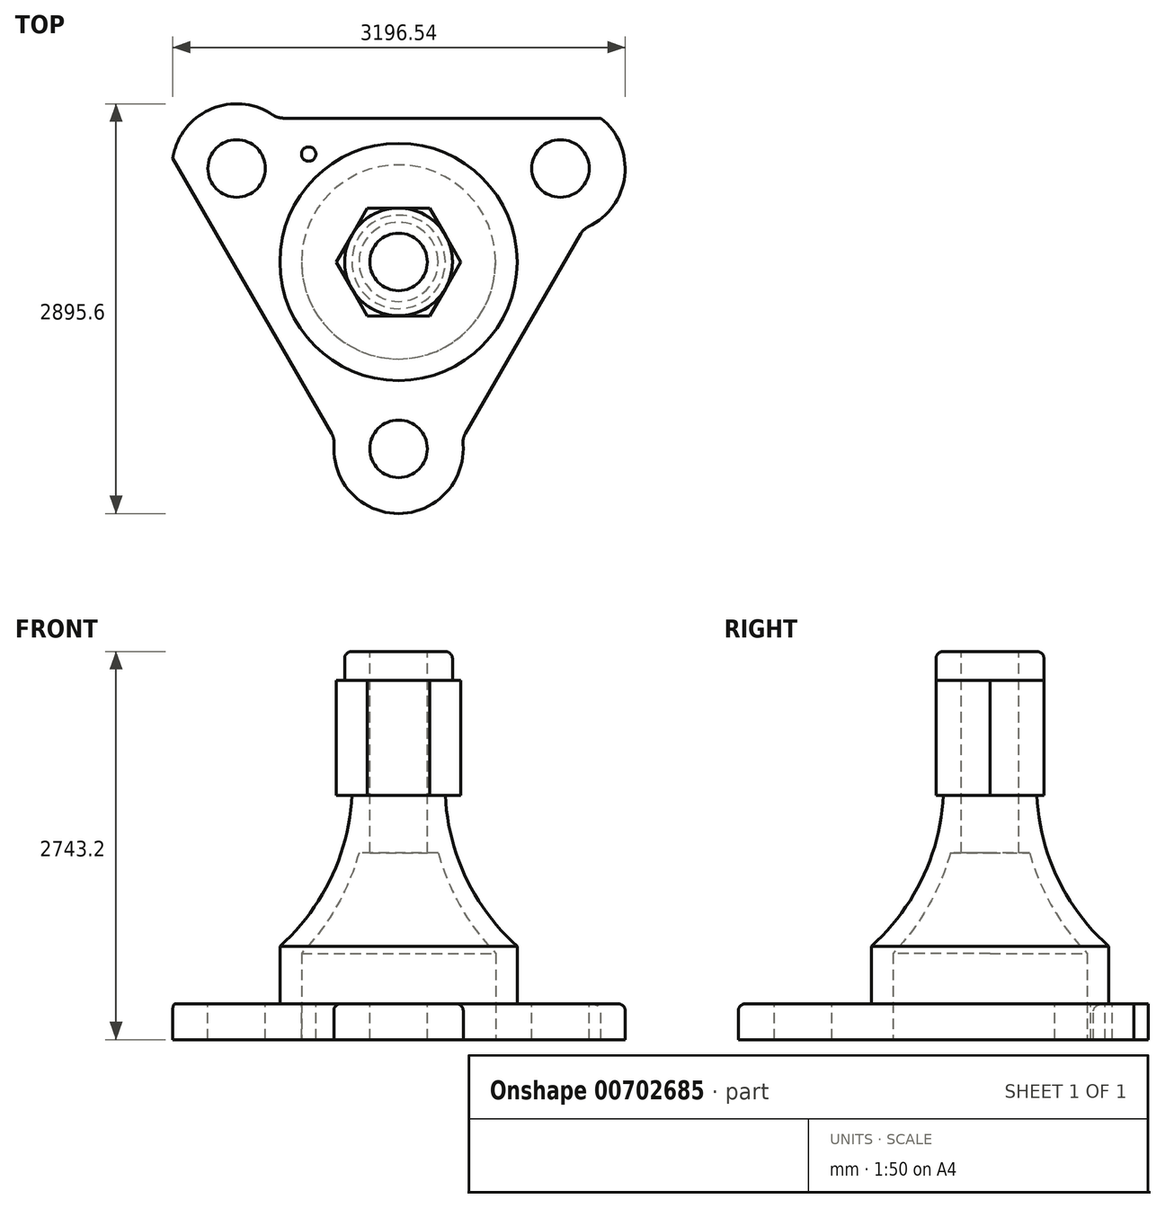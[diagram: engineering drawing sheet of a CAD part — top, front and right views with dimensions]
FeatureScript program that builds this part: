
annotation { "Feature Type Name" : "Feature", "Feature Type Description" : "" }
export const myFeature = defineFeature(function(context is Context, id is Id, definition is map)
    precondition{}
    {
        {
            var Q0;
            Q0=qCreatedBy(makeId("Top.planeOp"),FACE);
            var sketch = newSketch(context, id + "F0", { "sketchPlane" : qUnion([Q0])});
            skCircle(sketch, "E0.cCircle", {"center": v(0, 0) * mm, "radius": 2032 * mm, "construction": true});
            skLineSegment(sketch, "E0.0", {"start": v(0, -2032) * mm, "end": v(-1759.76, 1016) * mm});
            skLineSegment(sketch, "E0.1", {"start": v(-1759.76, 1016) * mm, "end": v(1759.76, 1016) * mm});
            skLineSegment(sketch, "E0.2", {"start": v(1759.76, 1016) * mm, "end": v(0, -2032) * mm});
            skSolve(sketch);
        }
        {
            var Q0;
            Q0 = qSketchRegion(id + "F0", true);
            extrude(context, id + "F1", {"entities" : qUnion([Q0]), "depth" : 254 * mm, "offsetDistance" : 25.4 * mm});
        }
        {
            var Q0;
            Q0=qCreatedBy(makeId("Front.planeOp"),FACE);
            var sketch = newSketch(context, id + "F2", { "sketchPlane" : qUnion([Q0])});
            skLineSegment(sketch, "E1", {"start": v(0, 0) * mm, "end": v(0, 944.42) * mm, "construction": true});
            skSolve(sketch);
        }
        {
            var Q0;
            Q0=makeQuery(id+"F1.opExtrude","CAP_FACE",FACE,{"disambiguationData":[OSD([sQuery(id+"F0.wireOp",EDGE,"E0.0"),sQuery(id+"F0.wireOp",EDGE,"E0.1"),sQuery(id+"F0.wireOp",EDGE,"E0.2")])],"isStart":false});
            var sketch = newSketch(context, id + "F3", { "sketchPlane" : qUnion([Q0])});
            skCircle(sketch, "E2", {"center": v(0, -1320.8) * mm, "radius": 457.2 * mm});
            skCircle(sketch, "E3.1.0", {"center": v(1143.85, 660.4) * mm, "radius": 457.2 * mm});
            skCircle(sketch, "E3.2.0", {"center": v(-1143.85, 660.4) * mm, "radius": 457.2 * mm});
            skPoint(sketch, "E3.center", {"position": v(0, 0) * mm});
            skSolve(sketch);
        }
        {
            var Q0;
            {var subQ0=sQuery(id+"F3.wireOp",EDGE,"E2");var subQ1=makeQuery(id+"F1.opExtrude","CAP_EDGE",EDGE,{"disambiguationData":[OSD([sQuery(id+"F0.wireOp",EDGE,"E0.0")])],"isStart":false});var subQ2=makeQuery(id+"F3.imprint","INTERSECT",VERTEX,{"disambiguationData":[OD(0.0)],"derivedFrom":[subQ1,subQ0]});Q0=makeQuery(id+"F3.imprint","IMPRINT",FACE,{"disambiguationData":[TD([[makeQuery(id+"F3.imprint","IMPRINT",EDGE,{"disambiguationData":[TD([[subQ2,1.0]])],"derivedFrom":subQ0}),1.0]])]});}
            var Q1;
            {var subQ0=sQuery(id+"F3.wireOp",EDGE,"E2");var subQ1=makeQuery(id+"F1.opExtrude","CAP_EDGE",EDGE,{"disambiguationData":[OSD([sQuery(id+"F0.wireOp",EDGE,"E0.2")])],"isStart":false});var subQ2=makeQuery(id+"F3.imprint","INTERSECT",VERTEX,{"disambiguationData":[OD(0.0)],"derivedFrom":[subQ1,subQ0]});Q1=makeQuery(id+"F3.imprint","IMPRINT",FACE,{"disambiguationData":[TD([[makeQuery(id+"F3.imprint","IMPRINT",EDGE,{"disambiguationData":[TD([[subQ2,1.0]])],"derivedFrom":subQ0}),1.0]])]});}
            var Q2;
            {var subQ0=sQuery(id+"F3.wireOp",EDGE,"E2");var subQ1=makeQuery(id+"F1.opExtrude","CAP_EDGE",EDGE,{"disambiguationData":[OSD([sQuery(id+"F0.wireOp",EDGE,"E0.0")])],"isStart":false});var subQ2=makeQuery(id+"F3.imprint","INTERSECT",VERTEX,{"disambiguationData":[OD(0.0)],"derivedFrom":[subQ1,subQ0]});Q2=makeQuery(id+"F3.imprint","IMPRINT",FACE,{"disambiguationData":[TD([[makeQuery(id+"F3.imprint","IMPRINT",EDGE,{"disambiguationData":[TD([[subQ2,-1.0]])],"derivedFrom":subQ0}),1.0]])]});}
            var Q3;
            {var subQ0=sQuery(id+"F3.wireOp",EDGE,"E3.1.0");var subQ1=makeQuery(id+"F1.opExtrude","CAP_EDGE",EDGE,{"disambiguationData":[OSD([sQuery(id+"F0.wireOp",EDGE,"E0.2")])],"isStart":false});var subQ2=makeQuery(id+"F3.imprint","INTERSECT",VERTEX,{"disambiguationData":[OD(0.0)],"derivedFrom":[subQ1,subQ0]});Q3=makeQuery(id+"F3.imprint","IMPRINT",FACE,{"disambiguationData":[TD([[makeQuery(id+"F3.imprint","IMPRINT",EDGE,{"disambiguationData":[TD([[subQ2,1.0]])],"derivedFrom":subQ0}),1.0]])]});}
            var Q4;
            {var subQ0=sQuery(id+"F3.wireOp",EDGE,"E3.1.0");var subQ1=makeQuery(id+"F1.opExtrude","CAP_EDGE",EDGE,{"disambiguationData":[OSD([sQuery(id+"F0.wireOp",EDGE,"E0.2")])],"isStart":false});var subQ2=makeQuery(id+"F3.imprint","INTERSECT",VERTEX,{"disambiguationData":[OD(0.0)],"derivedFrom":[subQ1,subQ0]});Q4=makeQuery(id+"F3.imprint","IMPRINT",FACE,{"disambiguationData":[TD([[makeQuery(id+"F3.imprint","IMPRINT",EDGE,{"disambiguationData":[TD([[subQ2,-1.0]])],"derivedFrom":subQ0}),1.0]])]});}
            var Q5;
            {var subQ0=sQuery(id+"F3.wireOp",EDGE,"E3.1.0");var subQ1=makeQuery(id+"F1.opExtrude","CAP_EDGE",EDGE,{"disambiguationData":[OSD([sQuery(id+"F0.wireOp",EDGE,"E0.1")])],"isStart":false});var subQ2=makeQuery(id+"F3.imprint","INTERSECT",VERTEX,{"disambiguationData":[OD(0.0)],"derivedFrom":[subQ1,subQ0]});Q5=makeQuery(id+"F3.imprint","IMPRINT",FACE,{"disambiguationData":[TD([[makeQuery(id+"F3.imprint","IMPRINT",EDGE,{"disambiguationData":[TD([[subQ2,1.0]])],"derivedFrom":subQ0}),1.0]])]});}
            var Q6;
            {var subQ0=sQuery(id+"F3.wireOp",EDGE,"E3.2.0");var subQ1=makeQuery(id+"F1.opExtrude","CAP_EDGE",EDGE,{"disambiguationData":[OSD([sQuery(id+"F0.wireOp",EDGE,"E0.1")])],"isStart":false});var subQ2=makeQuery(id+"F3.imprint","INTERSECT",VERTEX,{"disambiguationData":[OD(0.0)],"derivedFrom":[subQ1,subQ0]});Q6=makeQuery(id+"F3.imprint","IMPRINT",FACE,{"disambiguationData":[TD([[makeQuery(id+"F3.imprint","IMPRINT",EDGE,{"disambiguationData":[TD([[subQ2,1.0]])],"derivedFrom":subQ0}),1.0]])]});}
            var Q7;
            {var subQ0=sQuery(id+"F3.wireOp",EDGE,"E3.2.0");var subQ1=makeQuery(id+"F1.opExtrude","CAP_EDGE",EDGE,{"disambiguationData":[OSD([sQuery(id+"F0.wireOp",EDGE,"E0.1")])],"isStart":false});var subQ2=makeQuery(id+"F3.imprint","INTERSECT",VERTEX,{"disambiguationData":[OD(0.0)],"derivedFrom":[subQ1,subQ0]});Q7=makeQuery(id+"F3.imprint","IMPRINT",FACE,{"disambiguationData":[TD([[makeQuery(id+"F3.imprint","IMPRINT",EDGE,{"disambiguationData":[TD([[subQ2,-1.0]])],"derivedFrom":subQ0}),1.0]])]});}
            var Q8;
            {var subQ0=sQuery(id+"F3.wireOp",EDGE,"E3.2.0");var subQ1=makeQuery(id+"F1.opExtrude","CAP_EDGE",EDGE,{"disambiguationData":[OSD([sQuery(id+"F0.wireOp",EDGE,"E0.0")])],"isStart":false});var subQ2=makeQuery(id+"F3.imprint","INTERSECT",VERTEX,{"disambiguationData":[OD(0.0)],"derivedFrom":[subQ1,subQ0]});Q8=makeQuery(id+"F3.imprint","IMPRINT",FACE,{"disambiguationData":[TD([[makeQuery(id+"F3.imprint","IMPRINT",EDGE,{"disambiguationData":[TD([[subQ2,1.0]])],"derivedFrom":subQ0}),1.0]])]});}
            extrude(context, id + "F4", {"entities" : qUnion([Q0, Q1, Q2, Q3, Q4, Q5, Q6, Q7, Q8]), "operationType" : NewBodyOperationType.ADD, "oppositeDirection" : true, "depth" : 254 * mm, "offsetDistance" : 25.4 * mm});
        }
        {
            var Q0;
            Q0=makeQuery(id+"F4.boolean.opBoolean","MERGE",FACE,{"derivedFrom":[makeQuery(id+"F1.opExtrude","CAP_FACE",FACE,{"disambiguationData":[OSD([sQuery(id+"F0.wireOp",EDGE,"E0.0"),sQuery(id+"F0.wireOp",EDGE,"E0.1"),sQuery(id+"F0.wireOp",EDGE,"E0.2")])],"isStart":false}),makeQuery(id+"F4.opExtrude","CAP_FACE",FACE,{"disambiguationData":[OSD([sQuery(id+"F3.wireOp",EDGE,"E2")])],"isStart":true}),makeQuery(id+"F4.opExtrude","CAP_FACE",FACE,{"disambiguationData":[OSD([sQuery(id+"F3.wireOp",EDGE,"E3.1.0")])],"isStart":true}),makeQuery(id+"F4.opExtrude","CAP_FACE",FACE,{"disambiguationData":[OSD([sQuery(id+"F3.wireOp",EDGE,"E3.2.0")])],"isStart":true})]});
            var sketch = newSketch(context, id + "F5", { "sketchPlane" : qUnion([Q0])});
            skArc(sketch, "E4.0", {"start": v(-451.64, -1249.73) * mm, "mid": v(-395.95, -1549.4) * mm, "end": v(-164.27, -1747.47) * mm});
            skArc(sketch, "E5.0", {"start": v(164.27, -1747.47) * mm, "mid": v(395.95, -1549.4) * mm, "end": v(451.64, -1249.73) * mm});
            skCircle(sketch, "E6", {"center": v(0, -1320.8) * mm, "radius": 203.2 * mm});
            skLineSegment(sketch, "E7", {"start": v(-164.27, -1747.47) * mm, "end": v(-304.8, -2103.07) * mm});
            skLineSegment(sketch, "E8", {"start": v(-304.8, -2103.07) * mm, "end": v(304.8, -2103.07) * mm});
            skLineSegment(sketch, "E9", {"start": v(304.8, -2103.07) * mm, "end": v(164.27, -1747.47) * mm});
            skArc(sketch, "E10", {"start": v(-164.27, -1747.47) * mm, "mid": v(0, -1778) * mm, "end": v(164.27, -1747.47) * mm});
            skCircle(sketch, "E11.1.0", {"center": v(1143.85, 660.4) * mm, "radius": 203.2 * mm});
            skLineSegment(sketch, "E11.1.1", {"start": v(1973.71, 787.57) * mm, "end": v(1668.91, 1315.5) * mm});
            skLineSegment(sketch, "E11.1.2", {"start": v(1595.49, 731.47) * mm, "end": v(1973.71, 787.57) * mm});
            skArc(sketch, "E11.1.3", {"start": v(1595.49, 731.47) * mm, "mid": v(1539.8, 889) * mm, "end": v(1431.21, 1016) * mm});
            skLineSegment(sketch, "E11.1.4", {"start": v(1668.91, 1315.5) * mm, "end": v(1431.21, 1016) * mm});
            skCircle(sketch, "E11.2.0", {"center": v(-1143.85, 660.4) * mm, "radius": 203.2 * mm});
            skLineSegment(sketch, "E11.2.1", {"start": v(-1668.91, 1315.5) * mm, "end": v(-1973.71, 787.57) * mm});
            skLineSegment(sketch, "E11.2.2", {"start": v(-1431.21, 1016) * mm, "end": v(-1668.91, 1315.5) * mm});
            skArc(sketch, "E11.2.3", {"start": v(-1431.21, 1016) * mm, "mid": v(-1539.8, 889) * mm, "end": v(-1595.49, 731.47) * mm});
            skLineSegment(sketch, "E11.2.4", {"start": v(-1973.71, 787.57) * mm, "end": v(-1595.49, 731.47) * mm});
            skPoint(sketch, "E11.center", {"position": v(0, 0) * mm});
            skSolve(sketch);
        }
        {
            var Q0;
            Q0=makeQuery(id+"F5.imprint","IMPRINT",FACE,{"disambiguationData":[TD([[makeQuery(id+"F5.imprint","IMPRINT",EDGE,{"derivedFrom":sQuery(id+"F5.wireOp",EDGE,"E7")}),1.0]])]});
            var Q1;
            Q1=makeQuery(id+"F5.imprint","IMPRINT",FACE,{"disambiguationData":[TD([[makeQuery(id+"F5.imprint","IMPRINT",EDGE,{"derivedFrom":sQuery(id+"F5.wireOp",EDGE,"E10")}),-1.0]])]});
            var Q2;
            Q2=makeQuery(id+"F5.imprint","IMPRINT",FACE,{"disambiguationData":[TD([[makeQuery(id+"F5.imprint","IMPRINT",EDGE,{"derivedFrom":sQuery(id+"F5.wireOp",EDGE,"E6")}),1.0]])]});
            var Q3;
            Q3=makeQuery(id+"F5.imprint","IMPRINT",FACE,{"disambiguationData":[TD([[makeQuery(id+"F5.imprint","IMPRINT",EDGE,{"derivedFrom":sQuery(id+"F5.wireOp",EDGE,"E11.1.1")}),1.0]])]});
            var Q4;
            Q4=makeQuery(id+"F5.imprint","IMPRINT",FACE,{"disambiguationData":[TD([[makeQuery(id+"F5.imprint","IMPRINT",EDGE,{"derivedFrom":sQuery(id+"F5.wireOp",EDGE,"E11.1.3")}),-1.0]])]});
            var Q5;
            Q5=makeQuery(id+"F5.imprint","IMPRINT",FACE,{"disambiguationData":[TD([[makeQuery(id+"F5.imprint","IMPRINT",EDGE,{"derivedFrom":sQuery(id+"F5.wireOp",EDGE,"E11.1.0")}),1.0]])]});
            var Q6;
            Q6=makeQuery(id+"F5.imprint","IMPRINT",FACE,{"disambiguationData":[TD([[makeQuery(id+"F5.imprint","IMPRINT",EDGE,{"derivedFrom":sQuery(id+"F5.wireOp",EDGE,"E11.2.0")}),1.0]])]});
            var Q7;
            Q7=makeQuery(id+"F5.imprint","IMPRINT",FACE,{"disambiguationData":[TD([[makeQuery(id+"F5.imprint","IMPRINT",EDGE,{"derivedFrom":sQuery(id+"F5.wireOp",EDGE,"E11.2.1")}),1.0]])]});
            var Q8;
            Q8=makeQuery(id+"F5.imprint","IMPRINT",FACE,{"disambiguationData":[TD([[makeQuery(id+"F5.imprint","IMPRINT",EDGE,{"derivedFrom":sQuery(id+"F5.wireOp",EDGE,"E11.2.3")}),-1.0]])]});
            extrude(context, id + "F6", {"entities" : qUnion([Q0, Q1, Q2, Q3, Q4, Q5, Q6, Q7, Q8]), "operationType" : NewBodyOperationType.REMOVE, "endBound" : BoundingType.THROUGH_ALL, "oppositeDirection" : true, "depth" : 25.4 * mm, "offsetDistance" : 25.4 * mm});
        }
        {
            var Q0;
            Q0=makeQuery(id+"F4.boolean.opBoolean","MERGE",FACE,{"derivedFrom":[makeQuery(id+"F1.opExtrude","CAP_FACE",FACE,{"disambiguationData":[OSD([sQuery(id+"F0.wireOp",EDGE,"E0.0"),sQuery(id+"F0.wireOp",EDGE,"E0.1"),sQuery(id+"F0.wireOp",EDGE,"E0.2")])],"isStart":false}),makeQuery(id+"F4.opExtrude","CAP_FACE",FACE,{"disambiguationData":[OSD([sQuery(id+"F3.wireOp",EDGE,"E2")])],"isStart":true}),makeQuery(id+"F4.opExtrude","CAP_FACE",FACE,{"disambiguationData":[OSD([sQuery(id+"F3.wireOp",EDGE,"E3.1.0")])],"isStart":true}),makeQuery(id+"F4.opExtrude","CAP_FACE",FACE,{"disambiguationData":[OSD([sQuery(id+"F3.wireOp",EDGE,"E3.2.0")])],"isStart":true})]});
            var sketch = newSketch(context, id + "F7", { "sketchPlane" : qUnion([Q0])});
            skCircle(sketch, "E12", {"center": v(0, 0) * mm, "radius": 838.2 * mm});
            skSolve(sketch);
        }
        {
            var Q0;
            Q0 = qSketchRegion(id + "F7", true);
            extrude(context, id + "F8", {"entities" : qUnion([Q0]), "operationType" : NewBodyOperationType.ADD, "depth" : 406.4 * mm, "offsetDistance" : 25.4 * mm});
        }
        {
            var Q0;
            Q0=qCreatedBy(makeId("Right.planeOp"),FACE);
            var sketch = newSketch(context, id + "F9", { "sketchPlane" : qUnion([Q0])});
            skLineSegment(sketch, "E13", {"start": v(-838.2, 660.4) * mm, "end": v(0, 660.4) * mm});
            skLineSegment(sketch, "E14", {"start": v(0, 660.4) * mm, "end": v(0, 1727.2) * mm});
            skLineSegment(sketch, "E15", {"start": v(0, 1727.2) * mm, "end": v(-330.2, 1727.2) * mm});
            skArc(sketch, "E16", {"start": v(-838.2, 660.4) * mm, "mid": v(-476.6, 1142.56) * mm, "end": v(-330.2, 1727.2) * mm});
            skSolve(sketch);
        }
        {
            var Q0;
            Q0 = qSketchRegion(id + "F9", true);
            var Q1;
            Q1=sQuery(id+"F2.wireOp",EDGE,"E1");
            revolve(context, id + "F10", {"operationType" : NewBodyOperationType.ADD, "entities" : qUnion([Q0]), "axis" : qUnion([Q1]), "revolveType" : RevolveType.FULL});
        }
        {
            var Q0;
            Q0=makeQuery(id+"F10.opRevolve","SWEPT_FACE",FACE,{"disambiguationData":[OSD([sQuery(id+"F9.wireOp",EDGE,"E15")])]});
            var sketch = newSketch(context, id + "F11", { "sketchPlane" : qUnion([Q0])});
            skCircle(sketch, "E17.cCircle", {"center": v(0, 0) * mm, "radius": 439.94 * mm, "construction": true});
            skLineSegment(sketch, "E17.0", {"start": v(439.94, 0) * mm, "end": v(219.97, -381) * mm});
            skLineSegment(sketch, "E17.1", {"start": v(219.97, -381) * mm, "end": v(-219.97, -381) * mm});
            skLineSegment(sketch, "E17.2", {"start": v(-219.97, -381) * mm, "end": v(-439.94, 0) * mm});
            skLineSegment(sketch, "E17.3", {"start": v(-439.94, 0) * mm, "end": v(-219.97, 381) * mm});
            skLineSegment(sketch, "E17.4", {"start": v(-219.97, 381) * mm, "end": v(219.97, 381) * mm});
            skLineSegment(sketch, "E17.5", {"start": v(219.97, 381) * mm, "end": v(439.94, 0) * mm});
            skSolve(sketch);
        }
        {
            var Q0;
            Q0 = qSketchRegion(id + "F11", true);
            extrude(context, id + "F12", {"entities" : qUnion([Q0]), "operationType" : NewBodyOperationType.ADD, "depth" : 812.8 * mm, "offsetDistance" : 25.4 * mm});
        }
        {
            var Q0;
            Q0=makeQuery(id+"F12.opExtrude","CAP_FACE",FACE,{"disambiguationData":[OSD([sQuery(id+"F11.wireOp",EDGE,"E17.0"),sQuery(id+"F11.wireOp",EDGE,"E17.1"),sQuery(id+"F11.wireOp",EDGE,"E17.2"),sQuery(id+"F11.wireOp",EDGE,"E17.3"),sQuery(id+"F11.wireOp",EDGE,"E17.4"),sQuery(id+"F11.wireOp",EDGE,"E17.5")])],"isStart":false});
            var sketch = newSketch(context, id + "F13", { "sketchPlane" : qUnion([Q0])});
            skCircle(sketch, "E18", {"center": v(0, 0) * mm, "radius": 381 * mm});
            skSolve(sketch);
        }
        {
            var Q0;
            Q0 = qSketchRegion(id + "F13", true);
            extrude(context, id + "F14", {"entities" : qUnion([Q0]), "operationType" : NewBodyOperationType.ADD, "depth" : 203.2 * mm, "offsetDistance" : 25.4 * mm});
        }
        {
            var Q0;
            Q0=makeQuery(id+"F4.boolean.opBoolean","MERGE",FACE,{"derivedFrom":[makeQuery(id+"F1.opExtrude","CAP_FACE",FACE,{"disambiguationData":[OSD([sQuery(id+"F0.wireOp",EDGE,"E0.0"),sQuery(id+"F0.wireOp",EDGE,"E0.1"),sQuery(id+"F0.wireOp",EDGE,"E0.2")])],"isStart":true}),makeQuery(id+"F4.opExtrude","CAP_FACE",FACE,{"disambiguationData":[OSD([sQuery(id+"F3.wireOp",EDGE,"E2")])],"isStart":false}),makeQuery(id+"F4.opExtrude","CAP_FACE",FACE,{"disambiguationData":[OSD([sQuery(id+"F3.wireOp",EDGE,"E3.1.0")])],"isStart":false}),makeQuery(id+"F4.opExtrude","CAP_FACE",FACE,{"disambiguationData":[OSD([sQuery(id+"F3.wireOp",EDGE,"E3.2.0")])],"isStart":false})]});
            var sketch = newSketch(context, id + "F15", { "sketchPlane" : qUnion([Q0])});
            skCircle(sketch, "E19", {"center": v(0, 0) * mm, "radius": 685.8 * mm});
            skSolve(sketch);
        }
        {
            var Q0;
            Q0=makeQuery(id+"F15.imprint","IMPRINT",FACE,{"disambiguationData":[TD([[makeQuery(id+"F15.imprint","IMPRINT",EDGE,{"derivedFrom":sQuery(id+"F15.wireOp",EDGE,"E19")}),1.0]])]});
            extrude(context, id + "F16", {"entities" : qUnion([Q0]), "operationType" : NewBodyOperationType.REMOVE, "oppositeDirection" : true, "depth" : 609.6 * mm, "offsetDistance" : 25.4 * mm});
        }
        {
            var Q0;
            Q0=makeQuery(id+"F14.opExtrude","CAP_FACE",FACE,{"disambiguationData":[OSD([sQuery(id+"F13.wireOp",EDGE,"E18")])],"isStart":false});
            var sketch = newSketch(context, id + "F17", { "sketchPlane" : qUnion([Q0])});
            skCircle(sketch, "E20", {"center": v(0, 0) * mm, "radius": 203.2 * mm});
            skSolve(sketch);
        }
        {
            var Q0;
            Q0=makeQuery(id+"F17.imprint","IMPRINT",FACE,{"disambiguationData":[TD([[makeQuery(id+"F17.imprint","IMPRINT",EDGE,{"derivedFrom":sQuery(id+"F17.wireOp",EDGE,"E20")}),1.0]])]});
            extrude(context, id + "F18", {"entities" : qUnion([Q0]), "operationType" : NewBodyOperationType.REMOVE, "endBound" : BoundingType.THROUGH_ALL, "oppositeDirection" : true, "depth" : 25.4 * mm, "offsetDistance" : 25.4 * mm});
        }
        {
            var Q0;
            Q0=qCreatedBy(makeId("Right.planeOp"),FACE);
            var sketch = newSketch(context, id + "F19", { "sketchPlane" : qUnion([Q0])});
            skLineSegment(sketch, "E21", {"start": v(-279.4, 1320.8) * mm, "end": v(0, 1320.8) * mm});
            skLineSegment(sketch, "E22", {"start": v(0, 1320.8) * mm, "end": v(0, 609.6) * mm});
            skLineSegment(sketch, "E23", {"start": v(0, 609.6) * mm, "end": v(-685.8, 609.6) * mm});
            skArc(sketch, "E24", {"start": v(-685.8, 609.6) * mm, "mid": v(-438.5, 940) * mm, "end": v(-279.4, 1320.8) * mm});
            skSolve(sketch);
        }
        {
            var Q0;
            Q0 = qSketchRegion(id + "F19", true);
            var Q1;
            Q1=sQuery(id+"F2.wireOp",EDGE,"E1");
            revolve(context, id + "F20", {"operationType" : NewBodyOperationType.REMOVE, "entities" : qUnion([Q0]), "axis" : qUnion([Q1]), "revolveType" : RevolveType.FULL, "oppositeDirection" : true});
        }
        {
            var Q0;
            Q0=makeQuery(id+"F4.boolean.opBoolean","INTERSECT",EDGE,{"disambiguationData":[OD(1.0)],"derivedFrom":[makeQuery(id+"F1.opExtrude","SWEPT_FACE",FACE,{"disambiguationData":[OSD([sQuery(id+"F0.wireOp",EDGE,"E0.2")])]}),makeQuery(id+"F4.opExtrude","SWEPT_FACE",FACE,{"disambiguationData":[OSD([sQuery(id+"F3.wireOp",EDGE,"E2")])]})]});
            var Q1;
            Q1=makeQuery(id+"F4.boolean.opBoolean","INTERSECT",EDGE,{"disambiguationData":[OD(1.0)],"derivedFrom":[makeQuery(id+"F1.opExtrude","SWEPT_FACE",FACE,{"disambiguationData":[OSD([sQuery(id+"F0.wireOp",EDGE,"E0.2")])]}),makeQuery(id+"F4.opExtrude","SWEPT_FACE",FACE,{"disambiguationData":[OSD([sQuery(id+"F3.wireOp",EDGE,"E3.1.0")])]})]});
            var Q2;
            Q2=makeQuery(id+"F4.boolean.opBoolean","INTERSECT",EDGE,{"disambiguationData":[OD(1.0)],"derivedFrom":[makeQuery(id+"F1.opExtrude","SWEPT_FACE",FACE,{"disambiguationData":[OSD([sQuery(id+"F0.wireOp",EDGE,"E0.1")])]}),makeQuery(id+"F4.opExtrude","SWEPT_FACE",FACE,{"disambiguationData":[OSD([sQuery(id+"F3.wireOp",EDGE,"E3.1.0")])]})]});
            var Q3;
            Q3=makeQuery(id+"F4.boolean.opBoolean","INTERSECT",EDGE,{"disambiguationData":[OD(1.0)],"derivedFrom":[makeQuery(id+"F1.opExtrude","SWEPT_FACE",FACE,{"disambiguationData":[OSD([sQuery(id+"F0.wireOp",EDGE,"E0.1")])]}),makeQuery(id+"F4.opExtrude","SWEPT_FACE",FACE,{"disambiguationData":[OSD([sQuery(id+"F3.wireOp",EDGE,"E3.2.0")])]})]});
            var Q4;
            Q4=makeQuery(id+"F4.boolean.opBoolean","INTERSECT",EDGE,{"disambiguationData":[OD(1.0)],"derivedFrom":[makeQuery(id+"F1.opExtrude","SWEPT_FACE",FACE,{"disambiguationData":[OSD([sQuery(id+"F0.wireOp",EDGE,"E0.0")])]}),makeQuery(id+"F4.opExtrude","SWEPT_FACE",FACE,{"disambiguationData":[OSD([sQuery(id+"F3.wireOp",EDGE,"E3.2.0")])]})]});
            var Q5;
            Q5=makeQuery(id+"F4.boolean.opBoolean","INTERSECT",EDGE,{"disambiguationData":[OD(1.0)],"derivedFrom":[makeQuery(id+"F1.opExtrude","SWEPT_FACE",FACE,{"disambiguationData":[OSD([sQuery(id+"F0.wireOp",EDGE,"E0.0")])]}),makeQuery(id+"F4.opExtrude","SWEPT_FACE",FACE,{"disambiguationData":[OSD([sQuery(id+"F3.wireOp",EDGE,"E2")])]})]});
            var Q6;
            Q6=makeQuery(id+"F8.opExtrude","CAP_EDGE",EDGE,{"disambiguationData":[OSD([sQuery(id+"F7.wireOp",EDGE,"E12")])],"isStart":true});
            fillet(context, id + "F21", {"entities" : qUnion([Q0, Q1, Q2, Q3, Q4, Q5, Q6]), "radius" : 127 * mm, "tangentPropagation" : true, "allowEdgeOverflow" : false});
        }
        {
            var Q0;
            {var subQ0=sQuery(id+"F3.wireOp",EDGE,"E2");var subQ1=sQuery(id+"F0.wireOp",EDGE,"E0.2");var subQ2=sQuery(id+"F3.wireOp",EDGE,"E3.1.0");Q0=makeQuery(id+"F4.boolean.opBoolean","SPLIT",EDGE,{"disambiguationData":[TD([makeQuery(id+"F1.opExtrude","CAP_FACE",FACE,{"disambiguationData":[OSD([sQuery(id+"F0.wireOp",EDGE,"E0.0"),sQuery(id+"F0.wireOp",EDGE,"E0.1"),subQ1])],"isStart":false}),makeQuery(id+"F1.opExtrude","SWEPT_FACE",FACE,{"disambiguationData":[OSD([subQ1])]}),makeQuery(id+"F4.opExtrude","SWEPT_FACE",FACE,{"disambiguationData":[OSD([subQ0])]}),makeQuery(id+"F4.opExtrude","CAP_FACE",FACE,{"disambiguationData":[OSD([subQ0])],"isStart":true}),makeQuery(id+"F4.opExtrude","SWEPT_FACE",FACE,{"disambiguationData":[OSD([subQ2])]}),makeQuery(id+"F4.opExtrude","CAP_FACE",FACE,{"disambiguationData":[OSD([subQ2])],"isStart":true}),makeQuery(id+"F4.opExtrude","CAP_FACE",FACE,{"disambiguationData":[OSD([sQuery(id+"F3.wireOp",EDGE,"E3.2.0")])],"isStart":true})])],"derivedFrom":makeQuery(id+"F1.opExtrude","CAP_EDGE",EDGE,{"disambiguationData":[OSD([subQ1])],"isStart":false})});}
            var Q1;
            Q1=makeQuery(id+"F14.opExtrude","CAP_EDGE",EDGE,{"disambiguationData":[OSD([sQuery(id+"F13.wireOp",EDGE,"E18")])],"isStart":false});
            fillet(context, id + "F22", {"entities" : qUnion([Q0, Q1]), "radius" : 50.8 * mm, "tangentPropagation" : true, "allowEdgeOverflow" : false});
        }
        {
            var Q0;
            Q0=makeQuery(id+"F22.opFillet","SPLIT",FACE,{"disambiguationData":[OD(0.0)],"derivedFrom":makeQuery(id+"F4.boolean.opBoolean","MERGE",FACE,{"derivedFrom":[makeQuery(id+"F1.opExtrude","CAP_FACE",FACE,{"disambiguationData":[OSD([sQuery(id+"F0.wireOp",EDGE,"E0.0"),sQuery(id+"F0.wireOp",EDGE,"E0.1"),sQuery(id+"F0.wireOp",EDGE,"E0.2")])],"isStart":false}),makeQuery(id+"F4.opExtrude","CAP_FACE",FACE,{"disambiguationData":[OSD([sQuery(id+"F3.wireOp",EDGE,"E2")])],"isStart":true}),makeQuery(id+"F4.opExtrude","CAP_FACE",FACE,{"disambiguationData":[OSD([sQuery(id+"F3.wireOp",EDGE,"E3.1.0")])],"isStart":true}),makeQuery(id+"F4.opExtrude","CAP_FACE",FACE,{"disambiguationData":[OSD([sQuery(id+"F3.wireOp",EDGE,"E3.2.0")])],"isStart":true})]})});
            var sketch = newSketch(context, id + "F23", { "sketchPlane" : qUnion([Q0])});
            skCircle(sketch, "E25", {"center": v(-635, 762) * mm, "radius": 50.8 * mm});
            skSolve(sketch);
        }
        {
            var Q0;
            Q0=makeQuery(id+"F23.imprint","IMPRINT",FACE,{"disambiguationData":[TD([[makeQuery(id+"F23.imprint","IMPRINT",EDGE,{"derivedFrom":sQuery(id+"F23.wireOp",EDGE,"E25")}),1.0]])]});
            extrude(context, id + "F24", {"entities" : qUnion([Q0]), "operationType" : NewBodyOperationType.REMOVE, "endBound" : BoundingType.SYMMETRIC, "oppositeDirection" : true, "depth" : 685.8 * mm, "offsetDistance" : 25.4 * mm});
        }
    });
